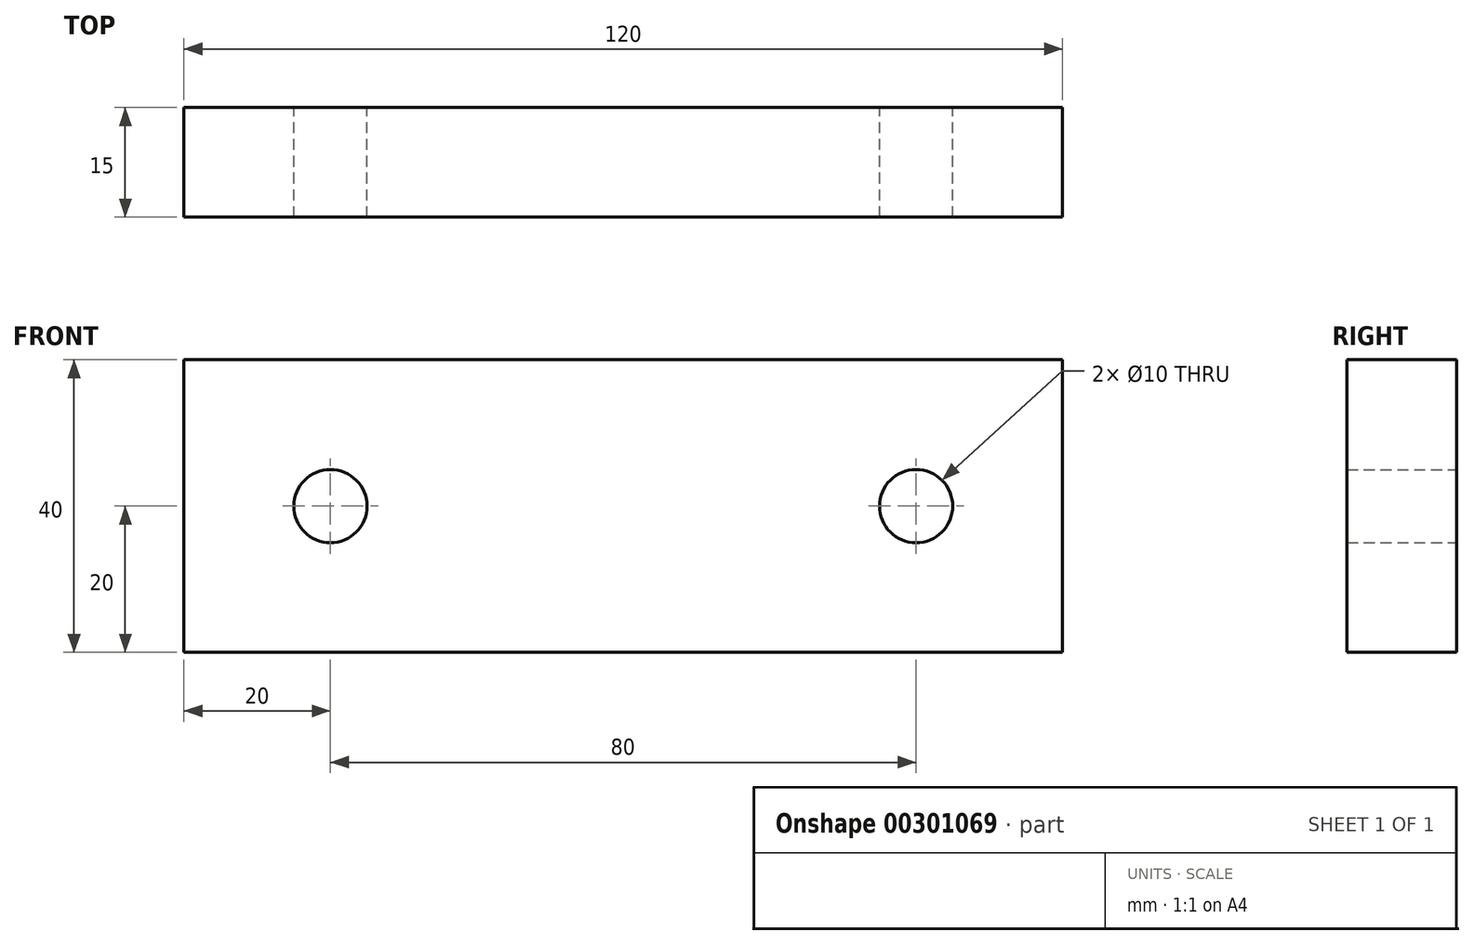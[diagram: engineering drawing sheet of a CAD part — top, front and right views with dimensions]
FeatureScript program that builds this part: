
annotation { "Feature Type Name" : "Feature", "Feature Type Description" : "" }
export const myFeature = defineFeature(function(context is Context, id is Id, definition is map)
    precondition{}
    {
        {
            var Q0;
            Q0=qCreatedBy(makeId("Front.planeOp"),FACE);
            var sketch = newSketch(context, id + "F0", { "sketchPlane" : qUnion([Q0])});
            skLineSegment(sketch, "E0", {"start": v(0, 0) * mm, "end": v(0, 40) * mm});
            skLineSegment(sketch, "E1", {"start": v(0, 40) * mm, "end": v(120, 40) * mm});
            skLineSegment(sketch, "E2", {"start": v(120, 40) * mm, "end": v(120, 0) * mm});
            skLineSegment(sketch, "E3", {"start": v(120, 0) * mm, "end": v(0, 0) * mm});
            skCircle(sketch, "E4", {"center": v(20, 20) * mm, "radius": 5 * mm});
            skCircle(sketch, "E5", {"center": v(100, 20) * mm, "radius": 5 * mm});
            skSolve(sketch);
        }
        {
            var Q0;
            Q0 = qSketchRegion(id + "F0", true);
            extrude(context, id + "F1", {"entities" : qUnion([Q0]), "depth" : 15 * mm});
        }
    });
